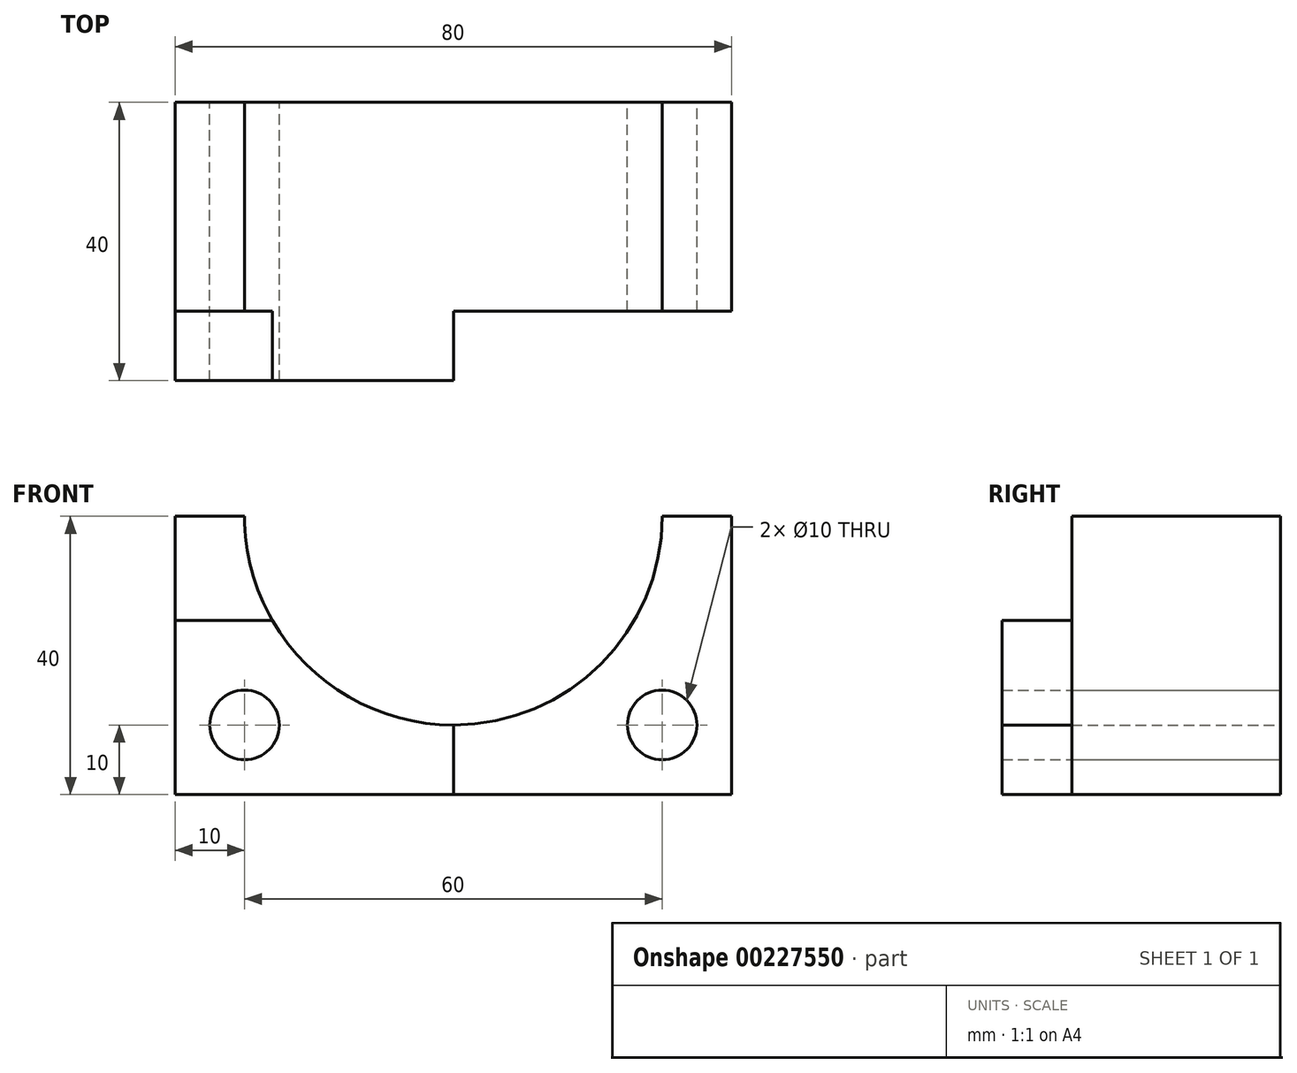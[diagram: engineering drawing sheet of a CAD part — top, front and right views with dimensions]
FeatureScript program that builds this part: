
annotation { "Feature Type Name" : "Feature", "Feature Type Description" : "" }
export const myFeature = defineFeature(function(context is Context, id is Id, definition is map)
    precondition{}
    {
        {
            var Q0;
            Q0=qCreatedBy(makeId("Front.planeOp"),FACE);
            var sketch = newSketch(context, id + "F0", { "sketchPlane" : qUnion([Q0])});
            skLineSegment(sketch, "E0", {"start": v(-40, 40) * mm, "end": v(-40, 0) * mm});
            skLineSegment(sketch, "E1", {"start": v(-40, 0) * mm, "end": v(40, 0) * mm});
            skLineSegment(sketch, "E2", {"start": v(40, 0) * mm, "end": v(40, 40) * mm});
            skLineSegment(sketch, "E3", {"start": v(40, 40) * mm, "end": v(30, 40) * mm});
            skLineSegment(sketch, "E4", {"start": v(-40, 40) * mm, "end": v(-30, 40) * mm});
            skArc(sketch, "E5", {"start": v(-30, 40) * mm, "mid": v(0, 10) * mm, "end": v(30, 40) * mm});
            skCircle(sketch, "E6", {"center": v(-30, 10) * mm, "radius": 5 * mm});
            skLineSegment(sketch, "E7", {"start": v(-40, 10) * mm, "end": v(40, 10) * mm, "construction": true});
            skCircle(sketch, "E8", {"center": v(30, 10) * mm, "radius": 5 * mm});
            skLineSegment(sketch, "E9", {"start": v(-40, 25) * mm, "end": v(-25.98, 25) * mm});
            skLineSegment(sketch, "E10", {"start": v(0, 10) * mm, "end": v(0, 0) * mm});
            skPoint(sketch, "E11", {"position": v(0, 0) * mm});
            skSolve(sketch);
        }
        {
            var Q0;
            {var subQ0=sQuery(id+"F0.wireOp",EDGE,"E4");Q0=makeQuery(id+"F0.imprint","IMPRINT",FACE,{"disambiguationData":[TD([[makeQuery(id+"F0.imprint","IMPRINT",EDGE,{"derivedFrom":subQ0}),-1.0]])]});}
            var Q1;
            {var subQ3=sQuery(id+"F0.wireOp",EDGE,"E2");Q1=makeQuery(id+"F0.imprint","IMPRINT",FACE,{"disambiguationData":[TD([[makeQuery(id+"F0.imprint","IMPRINT",EDGE,{"derivedFrom":subQ3}),1.0]])]});}
            extrude(context, id + "F1", {"entities" : qUnion([Q0, Q1]), "depth" : 30 * mm});
        }
        {
            var Q0;
            Q0=makeQuery(id+"F0.imprint","IMPRINT",FACE,{"disambiguationData":[TD([[makeQuery(id+"F0.imprint","IMPRINT",EDGE,{"derivedFrom":sQuery(id+"F0.wireOp",EDGE,"E6")}),-1.0]])]});
            extrude(context, id + "F2", {"entities" : qUnion([Q0]), "operationType" : NewBodyOperationType.ADD, "depth" : 40 * mm});
        }
    });
